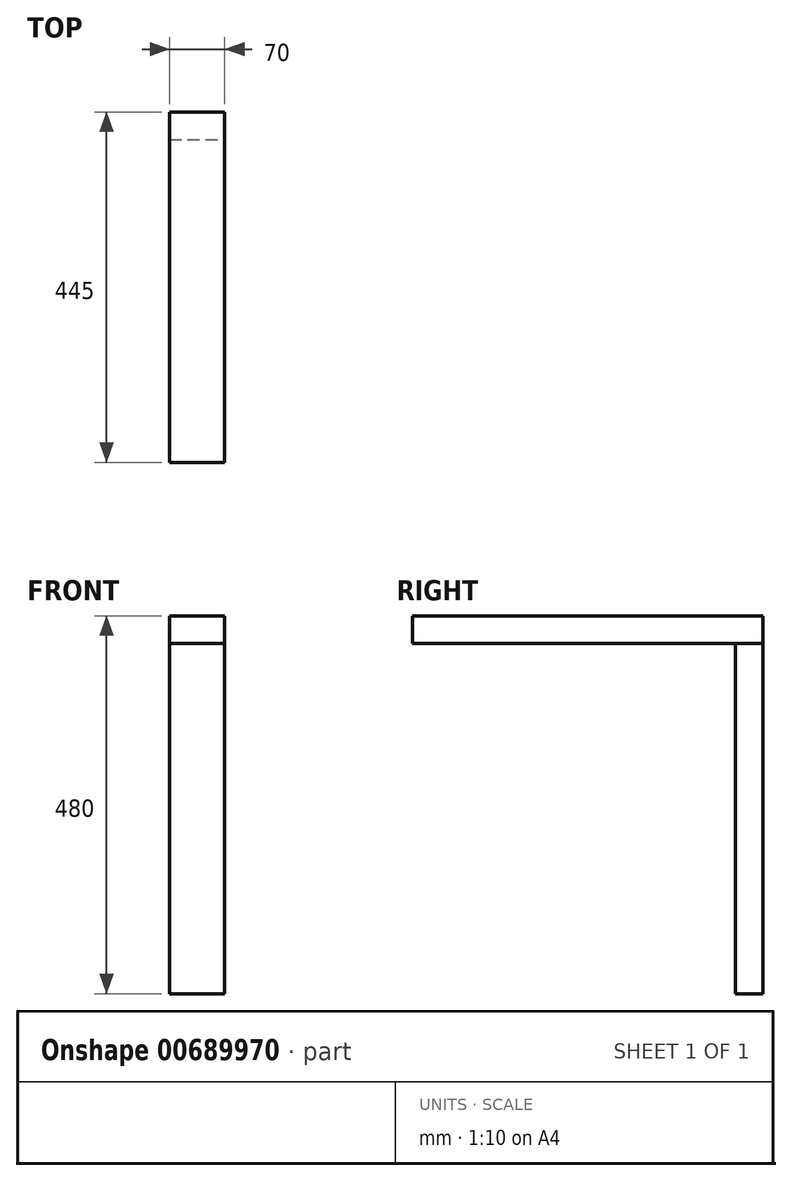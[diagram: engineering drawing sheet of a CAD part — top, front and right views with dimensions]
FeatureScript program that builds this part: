
annotation { "Feature Type Name" : "Feature", "Feature Type Description" : "" }
export const myFeature = defineFeature(function(context is Context, id is Id, definition is map)
    precondition{}
    {
        {
            var Q0;
            Q0=qCreatedBy(makeId("Front.planeOp"),FACE);
            var sketch = newSketch(context, id + "F0", { "sketchPlane" : qUnion([Q0])});
            skLineSegment(sketch, "E0.bottom", {"start": v(-35, -17.5) * mm, "end": v(35, -17.5) * mm});
            skLineSegment(sketch, "E0.top", {"start": v(-35, 17.5) * mm, "end": v(35, 17.5) * mm});
            skLineSegment(sketch, "E0.left", {"start": v(-35, -17.5) * mm, "end": v(-35, 17.5) * mm});
            skLineSegment(sketch, "E0.right", {"start": v(35, -17.5) * mm, "end": v(35, 17.5) * mm});
            skPoint(sketch, "E0.middle", {"position": v(0, 0) * mm});
            skSolve(sketch);
        }
        {
            var Q0;
            Q0=makeQuery(id+"F0.imprint","IMPRINT",FACE,{"disambiguationData":[TD([[makeQuery(id+"F0.imprint","IMPRINT",EDGE,{"derivedFrom":sQuery(id+"F0.wireOp",EDGE,"E0.bottom")}),1.0]])]});
            extrude(context, id + "F1", {"entities" : qUnion([Q0]), "depth" : 445 * mm, "offsetDistance" : 25 * mm});
        }
        {
            var Q0;
            Q0=makeQuery(id+"F1.opExtrude","SWEPT_FACE",FACE,{"disambiguationData":[OSD([sQuery(id+"F0.wireOp",EDGE,"E0.bottom")])]});
            var sketch = newSketch(context, id + "F2", { "sketchPlane" : qUnion([Q0])});
            skLineSegment(sketch, "E1.bottom", {"start": v(-35, 0) * mm, "end": v(35, 0) * mm});
            skLineSegment(sketch, "E1.top", {"start": v(-35, 35) * mm, "end": v(35, 35) * mm});
            skLineSegment(sketch, "E1.left", {"start": v(-35, 0) * mm, "end": v(-35, 35) * mm});
            skLineSegment(sketch, "E1.right", {"start": v(35, 0) * mm, "end": v(35, 35) * mm});
            skSolve(sketch);
        }
        {
            var Q0;
            Q0=makeQuery(id+"F2.imprint","IMPRINT",FACE,{"disambiguationData":[TD([[makeQuery(id+"F2.imprint","IMPRINT",EDGE,{"derivedFrom":sQuery(id+"F2.wireOp",EDGE,"E1.bottom")}),1.0]])]});
            extrude(context, id + "F3", {"entities" : qUnion([Q0]), "depth" : 445 * mm, "offsetDistance" : 25 * mm});
        }
    });
